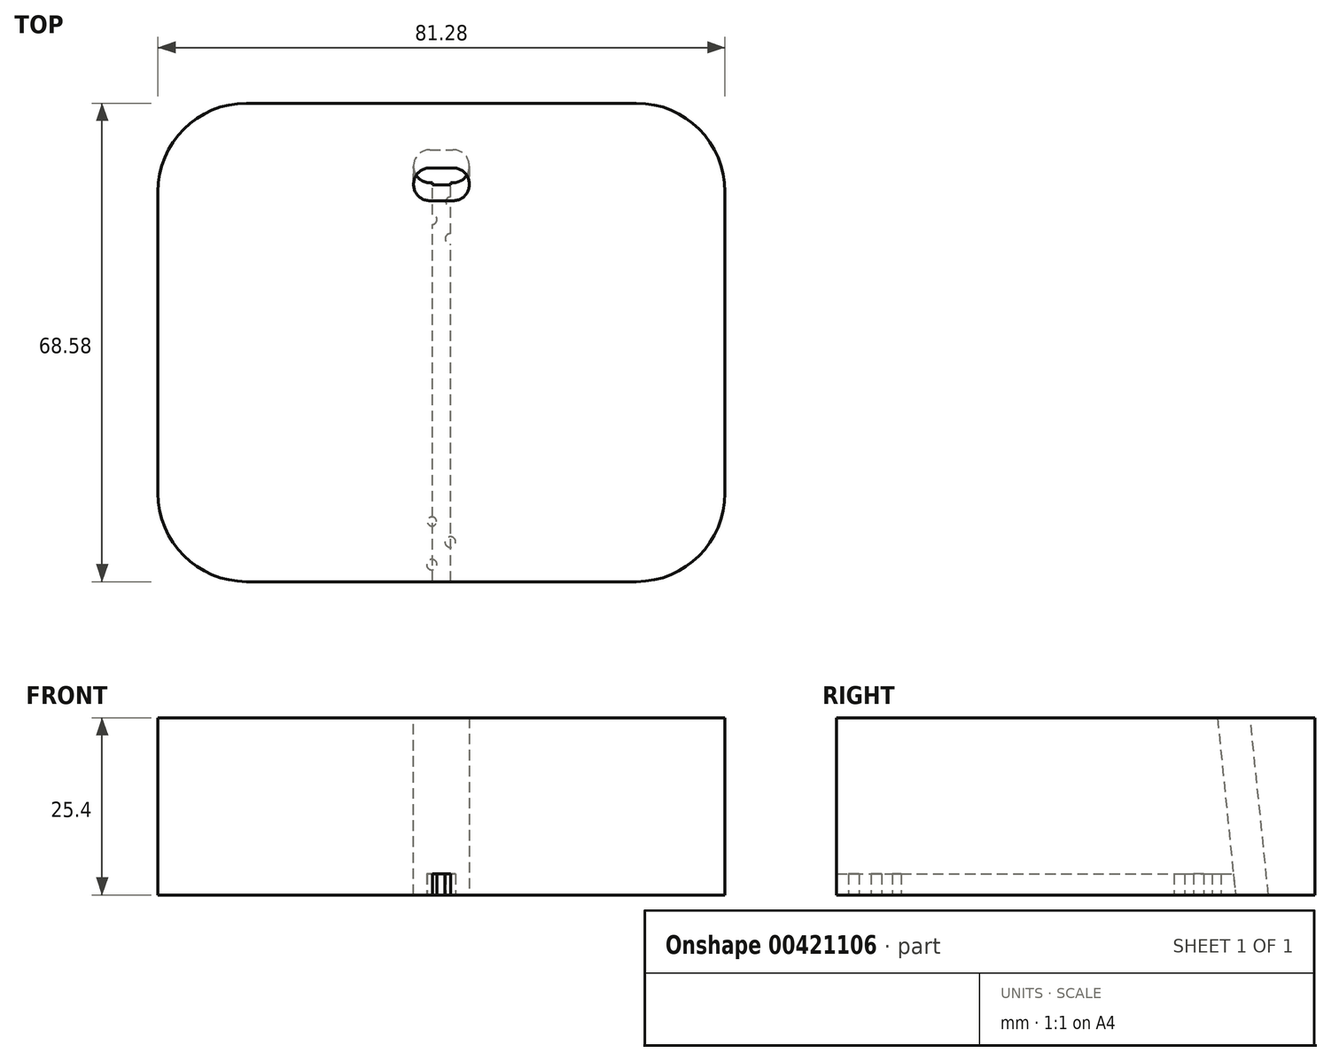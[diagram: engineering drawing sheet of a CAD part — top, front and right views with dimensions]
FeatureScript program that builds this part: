
annotation { "Feature Type Name" : "Feature", "Feature Type Description" : "" }
export const myFeature = defineFeature(function(context is Context, id is Id, definition is map)
    precondition{}
    {
        {
            var Q0;
            Q0=qCreatedBy(makeId("Top.planeOp"),FACE);
            var sketch = newSketch(context, id + "F0", { "sketchPlane" : qUnion([Q0])});
            skLineSegment(sketch, "E0.bottom", {"start": v(40.64, 34.3) * mm, "end": v(-40.64, 34.3) * mm});
            skLineSegment(sketch, "E0.top", {"start": v(40.64, -34.3) * mm, "end": v(-40.64, -34.3) * mm});
            skLineSegment(sketch, "E0.left", {"start": v(40.64, 34.3) * mm, "end": v(40.64, -34.3) * mm});
            skLineSegment(sketch, "E0.right", {"start": v(-40.64, 34.3) * mm, "end": v(-40.64, -34.3) * mm});
            skPoint(sketch, "E0.middle", {"position": v(0, 0) * mm});
            skSolve(sketch);
        }
        {
            var Q0;
            Q0=makeQuery(id+"F0.imprint","IMPRINT",FACE,{"disambiguationData":[TD([[makeQuery(id+"F0.imprint","IMPRINT",EDGE,{"derivedFrom":sQuery(id+"F0.wireOp",EDGE,"E0.bottom")}),1.0]])]});
            extrude(context, id + "F1", {"entities" : qUnion([Q0]), "depth" : 25.4 * mm});
        }
        {
            var Q0;
            Q0=makeQuery(id+"F1.opExtrude","SWEPT_EDGE",EDGE,{"disambiguationData":[OSD([sQuery(id+"F0.wireOp",EDGE,"E0.bottom"),sQuery(id+"F0.wireOp",EDGE,"E0.right")])]});
            var Q1;
            Q1=makeQuery(id+"F1.opExtrude","SWEPT_EDGE",EDGE,{"disambiguationData":[OSD([sQuery(id+"F0.wireOp",EDGE,"E0.bottom"),sQuery(id+"F0.wireOp",EDGE,"E0.left")])]});
            var Q2;
            Q2=makeQuery(id+"F1.opExtrude","SWEPT_EDGE",EDGE,{"disambiguationData":[OSD([sQuery(id+"F0.wireOp",EDGE,"E0.top"),sQuery(id+"F0.wireOp",EDGE,"E0.left")])]});
            var Q3;
            Q3=makeQuery(id+"F1.opExtrude","SWEPT_EDGE",EDGE,{"disambiguationData":[OSD([sQuery(id+"F0.wireOp",EDGE,"E0.top"),sQuery(id+"F0.wireOp",EDGE,"E0.right")])]});
            fillet(context, id + "F2", {"entities" : qUnion([Q0, Q1, Q2, Q3]), "radius" : 12.7 * mm, "tangentPropagation" : true, "allowEdgeOverflow" : false});
        }
        {
            var Q0;
            Q0=makeQuery(id+"F1.opExtrude","CAP_FACE",FACE,{"disambiguationData":[OSD([sQuery(id+"F0.wireOp",EDGE,"E0.bottom"),sQuery(id+"F0.wireOp",EDGE,"E0.top"),sQuery(id+"F0.wireOp",EDGE,"E0.left"),sQuery(id+"F0.wireOp",EDGE,"E0.right")])],"isStart":false});
            var sketch = newSketch(context, id + "F3", { "sketchPlane" : qUnion([Q0])});
            skLineSegment(sketch, "E1.bottom", {"start": v(4, 25) * mm, "end": v(-4, 25) * mm});
            skLineSegment(sketch, "E1.top", {"start": v(4, 20.3) * mm, "end": v(-4, 20.3) * mm});
            skLineSegment(sketch, "E1.left", {"start": v(4, 25) * mm, "end": v(4, 20.3) * mm});
            skLineSegment(sketch, "E1.right", {"start": v(-4, 25) * mm, "end": v(-4, 20.3) * mm});
            skPoint(sketch, "E1.middle", {"position": v(0, 22.66) * mm});
            skSolve(sketch);
        }
        {
            var Q0;
            Q0=makeQuery(id+"F1.opExtrude","CAP_FACE",FACE,{"disambiguationData":[OSD([sQuery(id+"F0.wireOp",EDGE,"E0.bottom"),sQuery(id+"F0.wireOp",EDGE,"E0.top"),sQuery(id+"F0.wireOp",EDGE,"E0.left"),sQuery(id+"F0.wireOp",EDGE,"E0.right")])],"isStart":true});
            var sketch = newSketch(context, id + "F4", { "sketchPlane" : qUnion([Q0])});
            skLineSegment(sketch, "E2.bottom", {"start": v(-4, -27.6) * mm, "end": v(4, -27.6) * mm});
            skLineSegment(sketch, "E2.top", {"start": v(-4, -22.9) * mm, "end": v(4, -22.9) * mm});
            skLineSegment(sketch, "E2.left", {"start": v(-4, -27.6) * mm, "end": v(-4, -22.9) * mm});
            skLineSegment(sketch, "E2.right", {"start": v(4, -27.6) * mm, "end": v(4, -22.9) * mm});
            skPoint(sketch, "E2.middle", {"position": v(0, -25.25) * mm});
            skSolve(sketch);
        }
        {
            var Q0;
            Q0=qCreatedBy(makeId("Right.planeOp"),FACE);
            var sketch = newSketch(context, id + "F5", { "sketchPlane" : qUnion([Q0])});
            skLineSegment(sketch, "E3", {"start": v(20.3, 25.41) * mm, "end": v(22.9, 0) * mm});
            skLineSegment(sketch, "E4", {"start": v(22.9, 0) * mm, "end": v(27.61, 0) * mm});
            skLineSegment(sketch, "E5", {"start": v(27.61, 0) * mm, "end": v(25, 25.45) * mm});
            skLineSegment(sketch, "E6", {"start": v(25, 25.45) * mm, "end": v(20.3, 25.41) * mm});
            skSolve(sketch);
        }
        {
            var Q0;
            Q0 = qSketchRegion(id + "F5", true);
            extrude(context, id + "F6", {"entities" : qUnion([Q0]), "operationType" : NewBodyOperationType.REMOVE, "oppositeDirection" : true, "depth" : 4 * mm});
        }
        {
            var Q0;
            Q0 = qSketchRegion(id + "F5", true);
            extrude(context, id + "F7", {"entities" : qUnion([Q0]), "operationType" : NewBodyOperationType.REMOVE, "oppositeDirection" : true, "depth" : -4 * mm});
        }
        {
            var Q0;
            Q0=makeQuery(id+"F7.boolean.opBoolean","COPY",EDGE,{"derivedFrom":makeQuery(id+"F7.opExtrude","CAP_EDGE",EDGE,{"disambiguationData":[OSD([sQuery(id+"F5.wireOp",EDGE,"E5")])],"isStart":false})});
            var Q1;
            Q1=makeQuery(id+"F7.boolean.opBoolean","COPY",EDGE,{"derivedFrom":makeQuery(id+"F7.opExtrude","CAP_EDGE",EDGE,{"disambiguationData":[OSD([sQuery(id+"F5.wireOp",EDGE,"E3")])],"isStart":false})});
            var Q2;
            Q2=makeQuery(id+"F6.boolean.opBoolean","COPY",EDGE,{"derivedFrom":makeQuery(id+"F6.opExtrude","CAP_EDGE",EDGE,{"disambiguationData":[OSD([sQuery(id+"F5.wireOp",EDGE,"E3")])],"isStart":false})});
            var Q3;
            Q3=makeQuery(id+"F6.boolean.opBoolean","COPY",EDGE,{"derivedFrom":makeQuery(id+"F6.opExtrude","CAP_EDGE",EDGE,{"disambiguationData":[OSD([sQuery(id+"F5.wireOp",EDGE,"E5")])],"isStart":false})});
            fillet(context, id + "F8", {"entities" : qUnion([Q0, Q1, Q2, Q3]), "radius" : 2.34 * mm, "tangentPropagation" : true, "allowEdgeOverflow" : false});
        }
        {
            var Q0;
            Q0=makeQuery(id+"F4.imprint","IMPRINT",FACE,{"disambiguationData":[TD([[makeQuery(id+"F4.imprint","IMPRINT",EDGE,{"derivedFrom":sQuery(id+"F4.wireOp",EDGE,"E2.bottom")}),-1.0]])]});
            var sketch = newSketch(context, id + "F9", { "sketchPlane" : qUnion([Q0])});
            skLineSegment(sketch, "E7.bottom", {"start": v(1.3, 39.89) * mm, "end": v(-1.3, 39.89) * mm});
            skLineSegment(sketch, "E7.top", {"start": v(1.3, -23.36) * mm, "end": v(-1.3, -23.36) * mm});
            skLineSegment(sketch, "E7.left", {"start": v(1.3, 39.89) * mm, "end": v(1.3, -23.36) * mm});
            skLineSegment(sketch, "E7.right", {"start": v(-1.3, 39.89) * mm, "end": v(-1.3, -23.36) * mm});
            skPoint(sketch, "E7.middle", {"position": v(0, 8.26) * mm});
            skSolve(sketch);
        }
        {
            var Q0;
            Q0 = qSketchRegion(id + "F9", true);
            extrude(context, id + "F10", {"entities" : qUnion([Q0]), "operationType" : NewBodyOperationType.REMOVE, "oppositeDirection" : true, "depth" : 3 * mm});
        }
        {
            var Q0;
            Q0=makeQuery(id+"F4.imprint","IMPRINT",FACE,{"disambiguationData":[TD([[makeQuery(id+"F4.imprint","IMPRINT",EDGE,{"derivedFrom":sQuery(id+"F4.wireOp",EDGE,"E2.bottom")}),-1.0]])]});
            var sketch = newSketch(context, id + "F11", { "sketchPlane" : qUnion([Q0])});
            skCircle(sketch, "E8", {"center": v(-1.35, -17.61) * mm, "radius": 0.7 * mm});
            skCircle(sketch, "E9", {"center": v(1.28, -14.84) * mm, "radius": 0.75 * mm});
            skCircle(sketch, "E10", {"center": v(1.28, -20.17) * mm, "radius": 0.66 * mm});
            skSolve(sketch);
        }
        {
            var Q0;
            Q0 = qSketchRegion(id + "F11", true);
            extrude(context, id + "F12", {"entities" : qUnion([Q0]), "operationType" : NewBodyOperationType.ADD, "depth" : -3 * mm});
        }
        {
            var Q0;
            Q0=makeQuery(id+"F4.imprint","IMPRINT",FACE,{"disambiguationData":[TD([[makeQuery(id+"F4.imprint","IMPRINT",EDGE,{"derivedFrom":sQuery(id+"F4.wireOp",EDGE,"E2.bottom")}),-1.0]])]});
            var sketch = newSketch(context, id + "F13", { "sketchPlane" : qUnion([Q0])});
            skCircle(sketch, "E11", {"center": v(-1.38, 31.85) * mm, "radius": 0.75 * mm});
            skCircle(sketch, "E12", {"center": v(1.27, 28.6) * mm, "radius": 0.76 * mm});
            skCircle(sketch, "E13", {"center": v(-1.36, 25.66) * mm, "radius": 0.66 * mm});
            skSolve(sketch);
        }
        {
            var Q0;
            Q0 = qSketchRegion(id + "F13", true);
            extrude(context, id + "F14", {"entities" : qUnion([Q0]), "depth" : -3 * mm});
        }
    });
